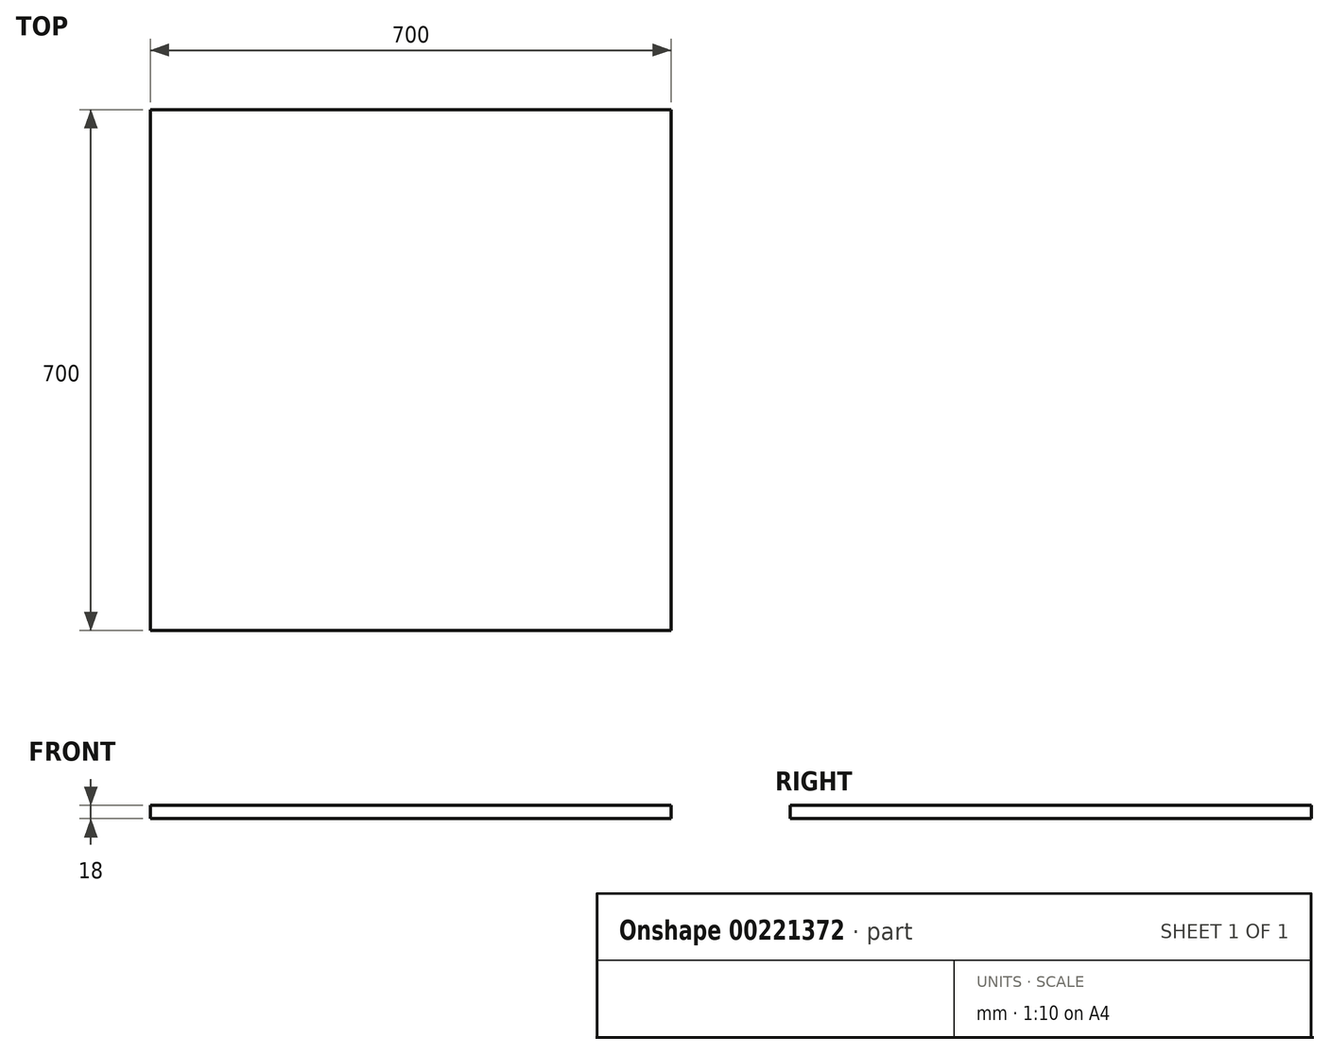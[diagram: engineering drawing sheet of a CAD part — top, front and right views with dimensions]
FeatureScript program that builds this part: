
annotation { "Feature Type Name" : "Feature", "Feature Type Description" : "" }
export const myFeature = defineFeature(function(context is Context, id is Id, definition is map)
    precondition{}
    {
        {
            var Q0;
            Q0=qCreatedBy(makeId("Top.planeOp"),FACE);
            var sketch = newSketch(context, id + "F0", { "sketchPlane" : qUnion([Q0])});
            skLineSegment(sketch, "E0.bottom", {"start": v(350, -350) * mm, "end": v(-350, -350) * mm});
            skLineSegment(sketch, "E0.top", {"start": v(350, 350) * mm, "end": v(-350, 350) * mm});
            skLineSegment(sketch, "E0.left", {"start": v(350, -350) * mm, "end": v(350, 350) * mm});
            skLineSegment(sketch, "E0.right", {"start": v(-350, -350) * mm, "end": v(-350, 350) * mm});
            skPoint(sketch, "E0.middle", {"position": v(0, 0) * mm});
            skSolve(sketch);
        }
        {
            var Q0;
            Q0 = qSketchRegion(id + "F0", true);
            extrude(context, id + "F1", {"entities" : qUnion([Q0]), "depth" : 18 * mm});
        }
    });
